# Revit family: DBLTD_TheSenatorGroup_OfficeChairs_Yoso_US
name_source: partatom
category: Furniture
units: mm (PartAtom-declared; Revit-internal decimal feet)

## family parameters
Always vertical = Yes
Cut with Voids When Loaded = No
OmniClass Number = 23.40.20.00
OmniClass Title = General Furniture and Specialties
Render Appearance Source = Family Geometry
Room Calculation Point = No
Shared = Yes
Work Plane-Based = No

## types (2) — shared parameters
Assembly Code = E2020200
AssetType = Movable
Category = Pr_40_50_12_57 Office chairs
DurationUnit = years
ExpectedLife = 5
FrameMaterial = DBLTD_TheSenatorGroup_Wood_Oak
Keynote = Pr_40_50_12_57 Office chairs
Manufacturer = The Senator Group
ManufacturerName = The Senator Group
ManufacturerURL = https://www.allermuir.com
Name = Chair
NominalDepth = 20 "
NominalHeight = 30 "
NominalWidth = 23 "
ProductInformation = https://www.allermuir.com
SeatingHeight = 18 "
Shape = Rectangular
Size = 30.25" x 22.75" x 20.25"
URL = https://www.thesenatorgroup.com
Uniclass2015Code = Pr_40_50_12_57
Uniclass2015Title = Office chairs
Uniclass2015Version = Products v1.15
Version = 1
WarrantyDescription = The Senator Group warrants that its manufactured products are free from manufacturing defects - in materials or workmanship - for a period of five (5) years.
WarrantyDurationLabor = 5
WarrantyDurationParts = 5
WarrantyDurationUnit = years
WarrantyGuarantorLabor = https://www.thesenatorgroup.com
WarrantyGuarantorParts = https://www.thesenatorgroup.com
zero-valued in all types: Cost, Default Elevation

## per-type parameters (varying)
| type | Color | Constituents | Finish | HasSolidOakSeat | HasUpholsteredSeatPad | Material | Model | ModelNumber |
| Armchair | Seat, Back and Frame: Solid Oak | Seat, Back and Frame | Seat, Back and Frame: Solid Oak | Yes | No | Seat, Back and Frame: Solid Oak | YOS101 | YOS101 |
| Armchair with Seat Pad | Seat, Back and Frame: Solid Oak. Seat Pad: Various | Seat, Back, Frame and Seat Pad | Seat, Back and Frame: Solid Oak. Seat Pad: Various | No | Yes | Seat, Back and Frame: Solid Oak. Seat Pad: Various | YOS101U1 | YOS101U1 |

note: column(s) folded — value = type name in every type: Description, ModelReference, Type Comments

## geometry (parser evidence)
native form markers: Sweep x2
no freeform markers — native parametric forms only
